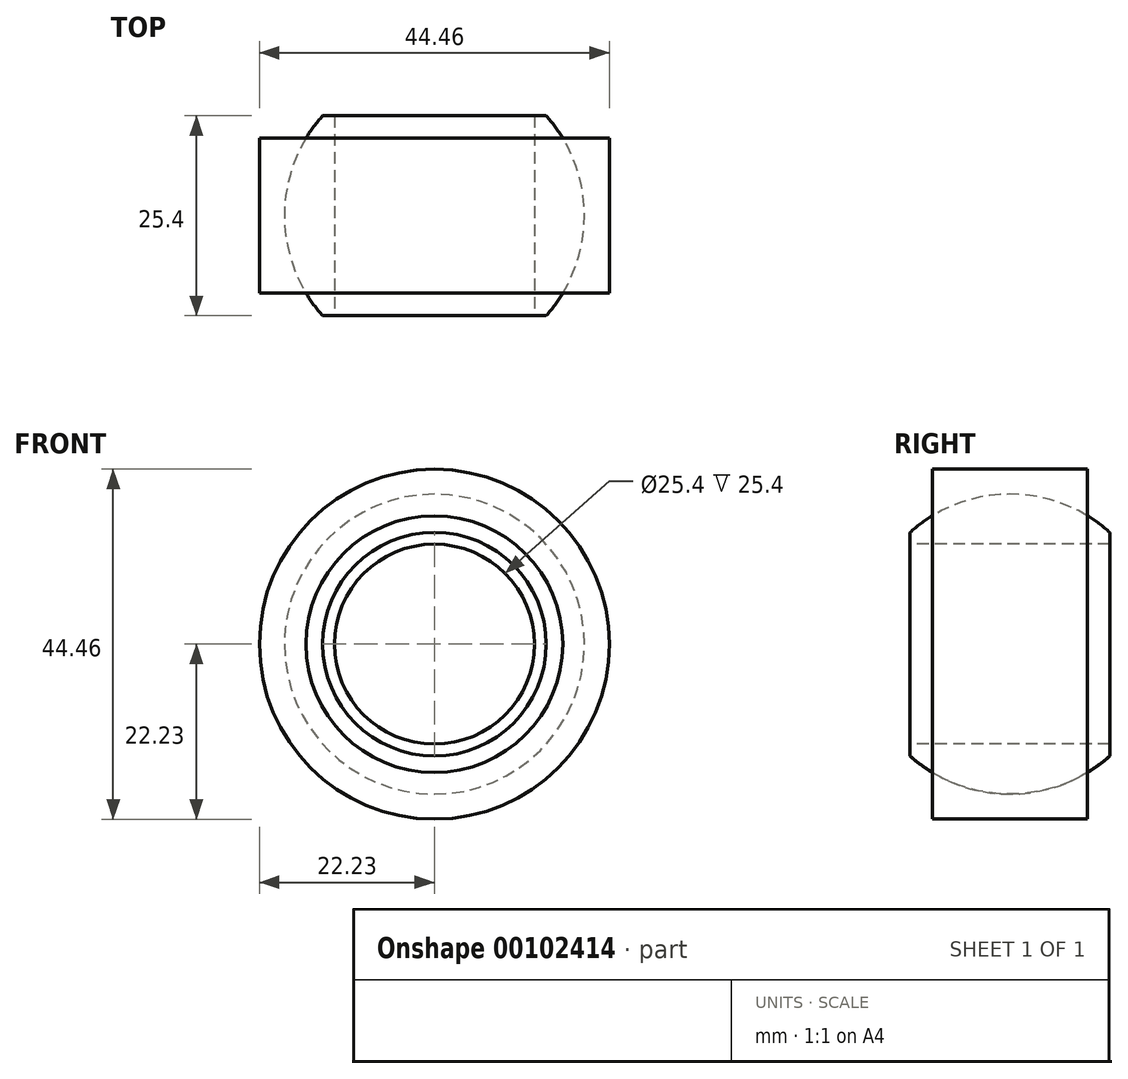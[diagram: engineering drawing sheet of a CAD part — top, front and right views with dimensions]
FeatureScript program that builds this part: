
annotation { "Feature Type Name" : "Feature", "Feature Type Description" : "" }
export const myFeature = defineFeature(function(context is Context, id is Id, definition is map)
    precondition{}
    {
        {
            var Q0;
            Q0=qCreatedBy(makeId("Right.planeOp"),FACE);
            var sketch = newSketch(context, id + "F0", { "sketchPlane" : qUnion([Q0])});
            skArc(sketch, "E0", {"start": v(12.7, 14.2) * mm, "mid": v(0, 19.05) * mm, "end": v(-12.7, 14.2) * mm});
            skLineSegment(sketch, "E1", {"start": v(-12.7, 14.2) * mm, "end": v(-12.7, 12.7) * mm});
            skLineSegment(sketch, "E2", {"start": v(12.7, 14.2) * mm, "end": v(12.7, 12.7) * mm});
            skLineSegment(sketch, "E3", {"start": v(-12.7, 12.7) * mm, "end": v(12.7, 12.7) * mm});
            skLineSegment(sketch, "E4", {"start": v(-9.84, 16.31) * mm, "end": v(-9.84, 22.23) * mm});
            skLineSegment(sketch, "E5", {"start": v(-9.84, 22.23) * mm, "end": v(9.84, 22.23) * mm});
            skLineSegment(sketch, "E6", {"start": v(9.84, 22.23) * mm, "end": v(9.84, 16.31) * mm});
            skLineSegment(sketch, "E7", {"start": v(-43.2, 0) * mm, "end": v(46.85, 0) * mm, "construction": true});
            skSolve(sketch);
        }
        {
            var Q0;
            {var subQ0=sQuery(id+"F0.wireOp",EDGE,"E1");Q0=makeQuery(id+"F0.imprint","IMPRINT",FACE,{"disambiguationData":[TD([[makeQuery(id+"F0.imprint","IMPRINT",EDGE,{"derivedFrom":subQ0}),1.0]])]});}
            var Q1;
            Q1=sQuery(id+"F0.wireOp",EDGE,"E7");
            revolve(context, id + "F1", {"entities" : qUnion([Q0]), "axis" : qUnion([Q1]), "revolveType" : RevolveType.FULL});
        }
        {
            var Q0;
            {var subQ0=sQuery(id+"F0.wireOp",EDGE,"E4");Q0=makeQuery(id+"F0.imprint","IMPRINT",FACE,{"disambiguationData":[TD([[makeQuery(id+"F0.imprint","IMPRINT",EDGE,{"derivedFrom":subQ0}),-1.0]])]});}
            var Q1;
            Q1=sQuery(id+"F0.wireOp",EDGE,"E7");
            revolve(context, id + "F2", {"entities" : qUnion([Q0]), "axis" : qUnion([Q1]), "revolveType" : RevolveType.FULL});
        }
    });
